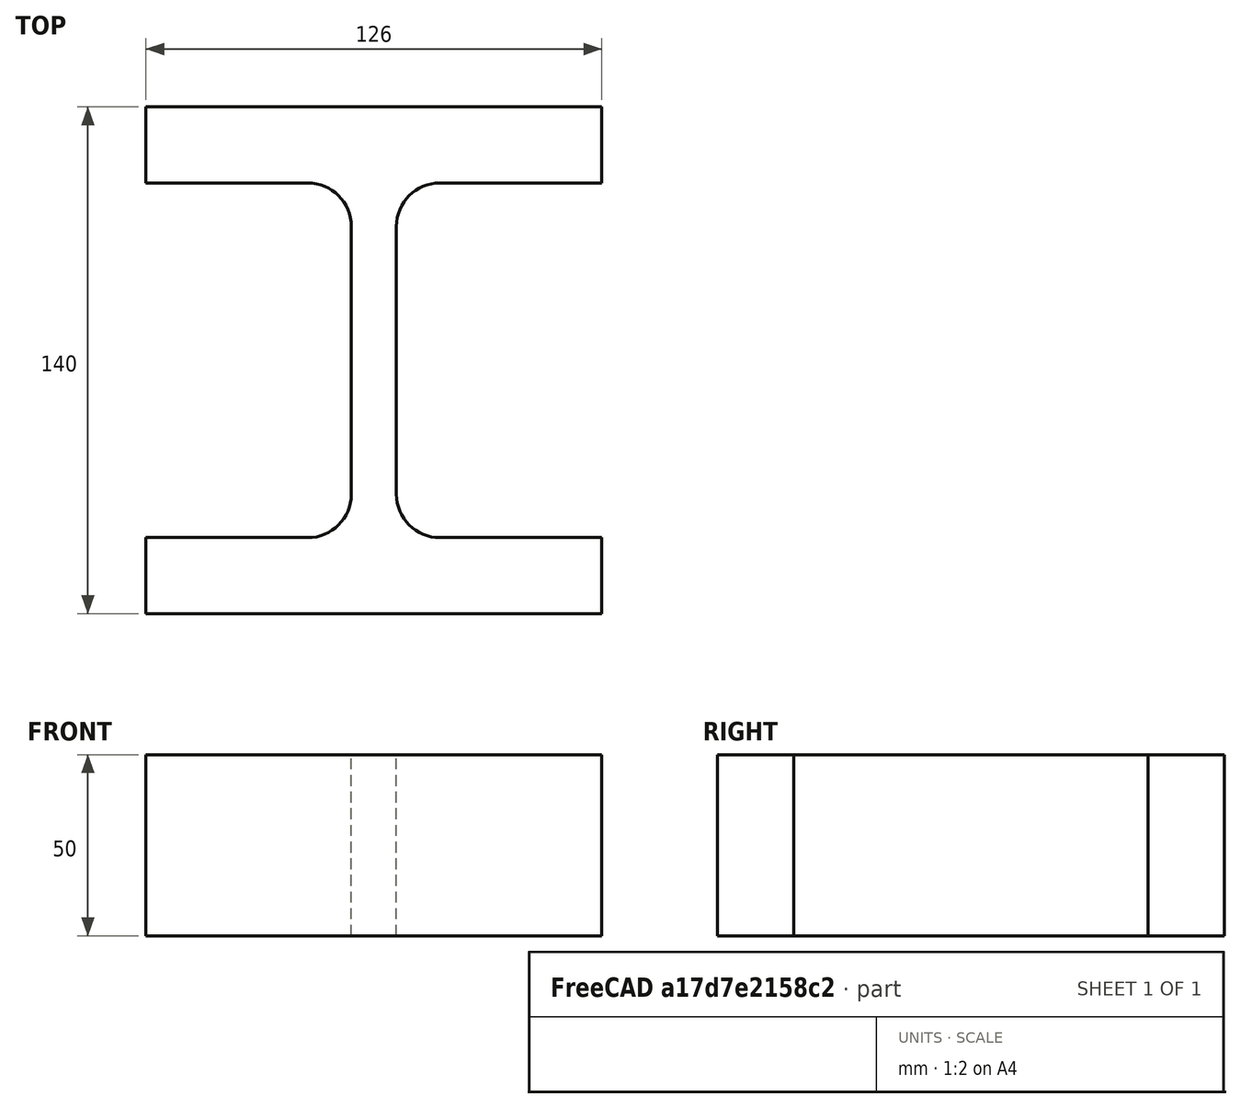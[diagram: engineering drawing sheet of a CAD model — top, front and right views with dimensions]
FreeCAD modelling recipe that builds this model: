
FCSTD DOCUMENT  (FreeCAD 0.15R4671 (Git))
Label: HE-M-Profile 120 DIN1025-4 S235JR
License: All rights reserved
LicenseURL: http://en.wikipedia.org/wiki/All_rights_reserved
objects: Sketcher::SketchObject×1, Part::Extrusion×1
note: 2 computed .brp shape members not serialized (recipe doc carries the construction recipe); baked Part::Feature solids carry a one-line shape summary decoded from their .brp

FEATURE [Sketcher::SketchObject] Sketch
  sketch-geometry (16):
    g0: LineSegment StartX=6.25 StartY=-37 StartZ=0 EndX=6.25 EndY=37 EndZ=0
    g1: LineSegment StartX=18.25 StartY=49 StartZ=0 EndX=63 EndY=49 EndZ=0
    g2: LineSegment StartX=63 StartY=49 StartZ=0 EndX=63 EndY=70 EndZ=0
    g3: LineSegment StartX=63 StartY=70 StartZ=0 EndX=-63 EndY=70 EndZ=0
    g4: LineSegment StartX=-63 StartY=70 StartZ=0 EndX=-63 EndY=49 EndZ=0
    g5: LineSegment StartX=-63 StartY=49 StartZ=0 EndX=-18.25 EndY=49 EndZ=0
    g6: LineSegment StartX=-6.25 StartY=37 StartZ=0 EndX=-6.25 EndY=-37 EndZ=0
    g7: LineSegment StartX=-18.25 StartY=-49 StartZ=0 EndX=-63 EndY=-49 EndZ=0
    g8: LineSegment StartX=-63 StartY=-49 StartZ=0 EndX=-63 EndY=-70 EndZ=0
    g9: LineSegment StartX=-63 StartY=-70 StartZ=0 EndX=63 EndY=-70 EndZ=0
    g10: LineSegment StartX=63 StartY=-70 StartZ=0 EndX=63 EndY=-49 EndZ=0
    g11: LineSegment StartX=63 StartY=-49 StartZ=0 EndX=18.25 EndY=-49 EndZ=0
    g12: ArcOfCircle CenterX=18.25 CenterY=37 CenterZ=0 NormalX=0 NormalY=0 NormalZ=1 Radius=12 StartAngle=1.5708 EndAngle=3.14159
    g13: ArcOfCircle CenterX=18.25 CenterY=-37 CenterZ=0 NormalX=0 NormalY=0 NormalZ=1 Radius=12 StartAngle=3.14159 EndAngle=4.71239
    g14: ArcOfCircle CenterX=-18.25 CenterY=37 CenterZ=0 NormalX=0 NormalY=0 NormalZ=1 Radius=12 StartAngle=0 EndAngle=1.5708
    g15: ArcOfCircle CenterX=-18.25 CenterY=-37 CenterZ=0 NormalX=0 NormalY=0 NormalZ=1 Radius=12 StartAngle=4.71239 EndAngle=6.28319
  constraints (42):
    c: Vertical(g0)
    c: Coincident(g2,g1)
    c: Vertical(g2)
    c: Coincident(g3,g2)
    c: Coincident(g4,g3)
    c: Vertical(g4)
    c: Coincident(g5,g4)
    c: Horizontal(g5)
    c: Vertical(g6)
    c: Horizontal(g7)
    c: Coincident(g8,g7)
    c: Vertical(g8)
    c: Coincident(g9,g8)
    c: Horizontal(g9)
    c: Coincident(g10,g9)
    c: Vertical(g10)
    c: Coincident(g11,g10)
    c: Horizontal(g11)
    c: Tangent(g1,g12) = 1.5708
    c: Tangent(g0,g12) = 1.5708
    c: Tangent(g0,g13) = 1.5708
    c: Tangent(g11,g13) = 1.5708
    c: Tangent(g5,g14) = 1.5708
    c: Tangent(g6,g14) = 1.5708
    c: Tangent(g6,g15) = 1.5708
    c: Tangent(g7,g15) = 1.5708
    c: Equal(g3,g9)
    c: Equal(g2,g4)
    c: Equal(g4,g8)
    c: Equal(g8,g10)
    c: Equal(g12,g14)
    c: Equal(g14,g15)
    c: Equal(g15,g13)
    c: Symmetric(g2,g3,g-2)
    c: Symmetric(g9,g8,g-2)
    c: Symmetric(g0,g6,g-2)
    c: Symmetric(g2,g9,g-1)
    c: DistanceY(g2,g9) = -140
    c: DistanceX(g3) = -126
    c: DistanceX(g0,g6) = -12.5
    c: DistanceY(g2) = 21
    c: Radius(g12) = 12
FEATURE [Part::Extrusion] Extrude  label="HE-M-Profile 120 DIN1025-4 S235JR"
  Base = -> Sketch
  Dir = (0,0,50)
  Solid = true
